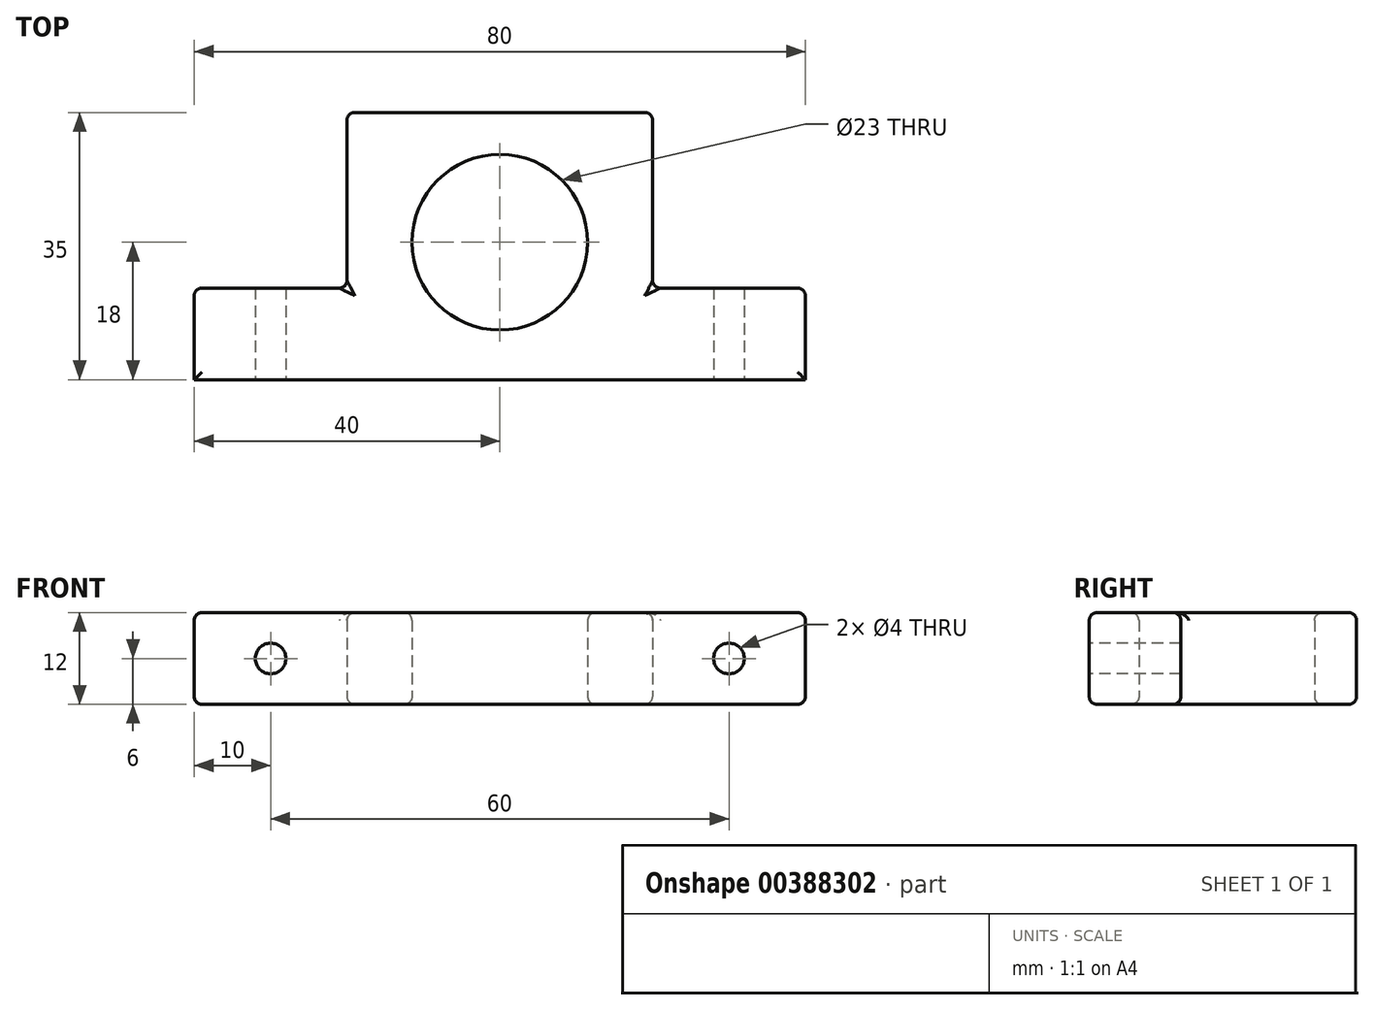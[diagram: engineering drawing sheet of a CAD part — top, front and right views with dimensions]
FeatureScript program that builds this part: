
annotation { "Feature Type Name" : "Feature", "Feature Type Description" : "" }
export const myFeature = defineFeature(function(context is Context, id is Id, definition is map)
    precondition{}
    {
        {
            var Q0;
            Q0=qCreatedBy(makeId("Top.planeOp"),FACE);
            var sketch = newSketch(context, id + "F0", { "sketchPlane" : qUnion([Q0])});
            skLineSegment(sketch, "E0", {"start": v(40, 0) * mm, "end": v(40, 12) * mm});
            skLineSegment(sketch, "E1", {"start": v(40, 12) * mm, "end": v(20, 12) * mm});
            skLineSegment(sketch, "E2", {"start": v(20, 12) * mm, "end": v(20, 35) * mm});
            skLineSegment(sketch, "E3", {"start": v(20, 35) * mm, "end": v(-20, 35) * mm});
            skLineSegment(sketch, "E4", {"start": v(-20, 35) * mm, "end": v(-20, 12) * mm});
            skLineSegment(sketch, "E5", {"start": v(-20, 12) * mm, "end": v(-40, 12) * mm});
            skLineSegment(sketch, "E6", {"start": v(-40, 12) * mm, "end": v(-40, 0) * mm});
            skLineSegment(sketch, "E7", {"start": v(-40, 0) * mm, "end": v(40, 0) * mm});
            skCircle(sketch, "E8", {"center": v(0, 18) * mm, "radius": 11.5 * mm});
            skSolve(sketch);
        }
        {
            var Q0;
            Q0=makeQuery(id+"F0.imprint","IMPRINT",FACE,{"disambiguationData":[TD([[makeQuery(id+"F0.imprint","IMPRINT",EDGE,{"derivedFrom":sQuery(id+"F0.wireOp",EDGE,"E0")}),1.0]])]});
            extrude(context, id + "F1", {"entities" : qUnion([Q0]), "flatOperationType" : FlatOperationType.REMOVE, "offsetDistance" : 25 * mm, "depth" : 12 * mm, "domain" : OperationDomain.MODEL});
        }
        {
            var Q0;
            Q0=makeQuery(id+"F1.opExtrude","SWEPT_FACE",FACE,{"disambiguationData":[OSD([sQuery(id+"F0.wireOp",EDGE,"E7")])]});
            var sketch = newSketch(context, id + "F2", { "sketchPlane" : qUnion([Q0])});
            skCircle(sketch, "E9", {"center": v(-30, 6) * mm, "radius": 2 * mm});
            skCircle(sketch, "E10", {"center": v(30, 6) * mm, "radius": 2 * mm});
            skSolve(sketch);
        }
        {
            var Q0;
            Q0 = qSketchRegion(id + "F2", true);
            extrude(context, id + "F3", {"entities" : qUnion([Q0]), "operationType" : NewBodyOperationType.REMOVE, "oppositeDirection" : true, "depth" : 25.5 * mm});
        }
        {
            var Q0;
            Q0=makeQuery(id+"F1.opExtrude","CAP_EDGE",EDGE,{"disambiguationData":[OSD([sQuery(id+"F0.wireOp",EDGE,"E6")])],"isStart":false});
            var Q1;
            Q1=makeQuery(id+"F1.opExtrude","CAP_EDGE",EDGE,{"disambiguationData":[OSD([sQuery(id+"F0.wireOp",EDGE,"E5")])],"isStart":false});
            var Q2;
            Q2=makeQuery(id+"F1.opExtrude","CAP_FACE",FACE,{"disambiguationData":[OSD([sQuery(id+"F0.wireOp",EDGE,"E0"),sQuery(id+"F0.wireOp",EDGE,"E1"),sQuery(id+"F0.wireOp",EDGE,"E2"),sQuery(id+"F0.wireOp",EDGE,"E3"),sQuery(id+"F0.wireOp",EDGE,"E4"),sQuery(id+"F0.wireOp",EDGE,"E5"),sQuery(id+"F0.wireOp",EDGE,"E6"),sQuery(id+"F0.wireOp",EDGE,"E7"),sQuery(id+"F0.wireOp",EDGE,"E8")])],"isStart":false});
            fillet(context, id + "F4", {"entities" : qUnion([Q0, Q1, Q2]), "radius" : 1 * mm, "tangentPropagation" : true, "allowEdgeOverflow" : false});
        }
        {
            var Q0;
            Q0=makeQuery(id+"F1.opExtrude","CAP_FACE",FACE,{"disambiguationData":[OSD([sQuery(id+"F0.wireOp",EDGE,"E0"),sQuery(id+"F0.wireOp",EDGE,"E1"),sQuery(id+"F0.wireOp",EDGE,"E2"),sQuery(id+"F0.wireOp",EDGE,"E3"),sQuery(id+"F0.wireOp",EDGE,"E4"),sQuery(id+"F0.wireOp",EDGE,"E5"),sQuery(id+"F0.wireOp",EDGE,"E6"),sQuery(id+"F0.wireOp",EDGE,"E7"),sQuery(id+"F0.wireOp",EDGE,"E8")])],"isStart":true});
            var Q1;
            Q1=makeQuery(id+"F1.opExtrude","SWEPT_EDGE",EDGE,{"disambiguationData":[OSD([sQuery(id+"F0.wireOp",EDGE,"E5"),sQuery(id+"F0.wireOp",EDGE,"E6")])]});
            var Q2;
            Q2=makeQuery(id+"F1.opExtrude","SWEPT_EDGE",EDGE,{"disambiguationData":[OSD([sQuery(id+"F0.wireOp",EDGE,"E4"),sQuery(id+"F0.wireOp",EDGE,"E5")])]});
            var Q3;
            Q3=makeQuery(id+"F1.opExtrude","SWEPT_EDGE",EDGE,{"disambiguationData":[OSD([sQuery(id+"F0.wireOp",EDGE,"E3"),sQuery(id+"F0.wireOp",EDGE,"E4")])]});
            var Q4;
            Q4=makeQuery(id+"F1.opExtrude","SWEPT_EDGE",EDGE,{"disambiguationData":[OSD([sQuery(id+"F0.wireOp",EDGE,"E0"),sQuery(id+"F0.wireOp",EDGE,"E1")])]});
            var Q5;
            Q5=makeQuery(id+"F1.opExtrude","SWEPT_FACE",FACE,{"disambiguationData":[OSD([sQuery(id+"F0.wireOp",EDGE,"E2")])]});
            fillet(context, id + "F5", {"entities" : qUnion([Q0, Q1, Q2, Q3, Q4, Q5]), "radius" : 1 * mm, "tangentPropagation" : true, "allowEdgeOverflow" : false});
        }
    });
